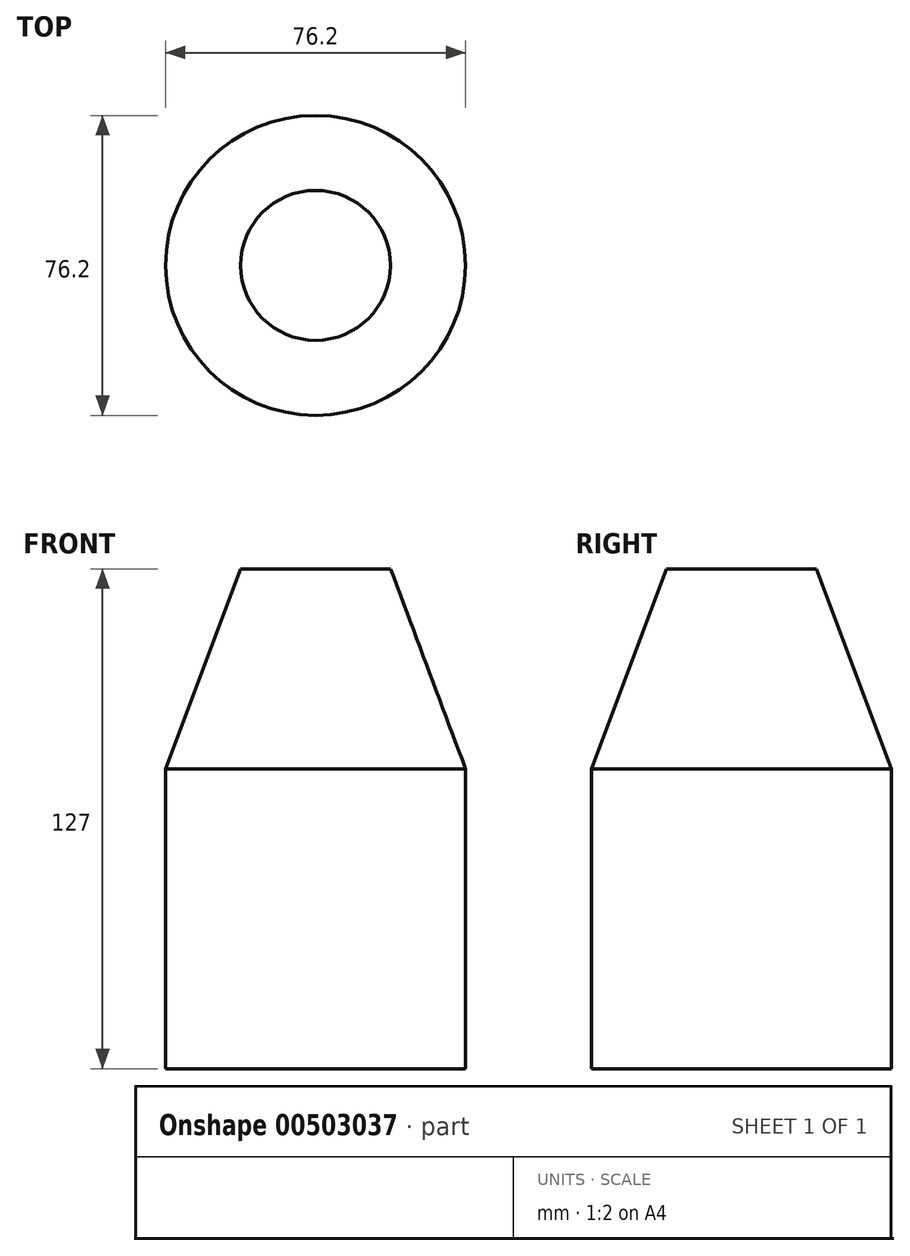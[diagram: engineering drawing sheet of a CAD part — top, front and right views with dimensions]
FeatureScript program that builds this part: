
annotation { "Feature Type Name" : "Feature", "Feature Type Description" : "" }
export const myFeature = defineFeature(function(context is Context, id is Id, definition is map)
    precondition{}
    {
        {
            var Q0;
            Q0=qCreatedBy(makeId("Front.planeOp"),FACE);
            var sketch = newSketch(context, id + "F0", { "sketchPlane" : qUnion([Q0])});
            skLineSegment(sketch, "E0", {"start": v(0, -26.82) * mm, "end": v(-38.1, -26.82) * mm});
            skLineSegment(sketch, "E1", {"start": v(-38.1, -26.82) * mm, "end": v(-38.1, 49.38) * mm});
            skLineSegment(sketch, "E2", {"start": v(-38.1, 49.38) * mm, "end": v(-19.05, 100.18) * mm});
            skLineSegment(sketch, "E3", {"start": v(-19.05, 100.18) * mm, "end": v(0, 100.18) * mm});
            skLineSegment(sketch, "E4", {"start": v(0, 100.18) * mm, "end": v(0, -26.82) * mm});
            skSolve(sketch);
        }
        {
            var Q0;
            Q0=qCreatedBy(makeId("Front.planeOp"),FACE);
            var sketch = newSketch(context, id + "F1", { "sketchPlane" : qUnion([Q0])});
            skLineSegment(sketch, "E5", {"start": v(0, 104.1) * mm, "end": v(0, -40.01) * mm, "construction": true});
            skSolve(sketch);
        }
        {
            var Q0;
            Q0 = qSketchRegion(id + "F0", true);
            var Q1;
            Q1=sQuery(id+"F1.wireOp",EDGE,"E5");
            revolve(context, id + "F2", {"entities" : qUnion([Q0]), "axis" : qUnion([Q1]), "revolveType" : RevolveType.FULL});
        }
    });
